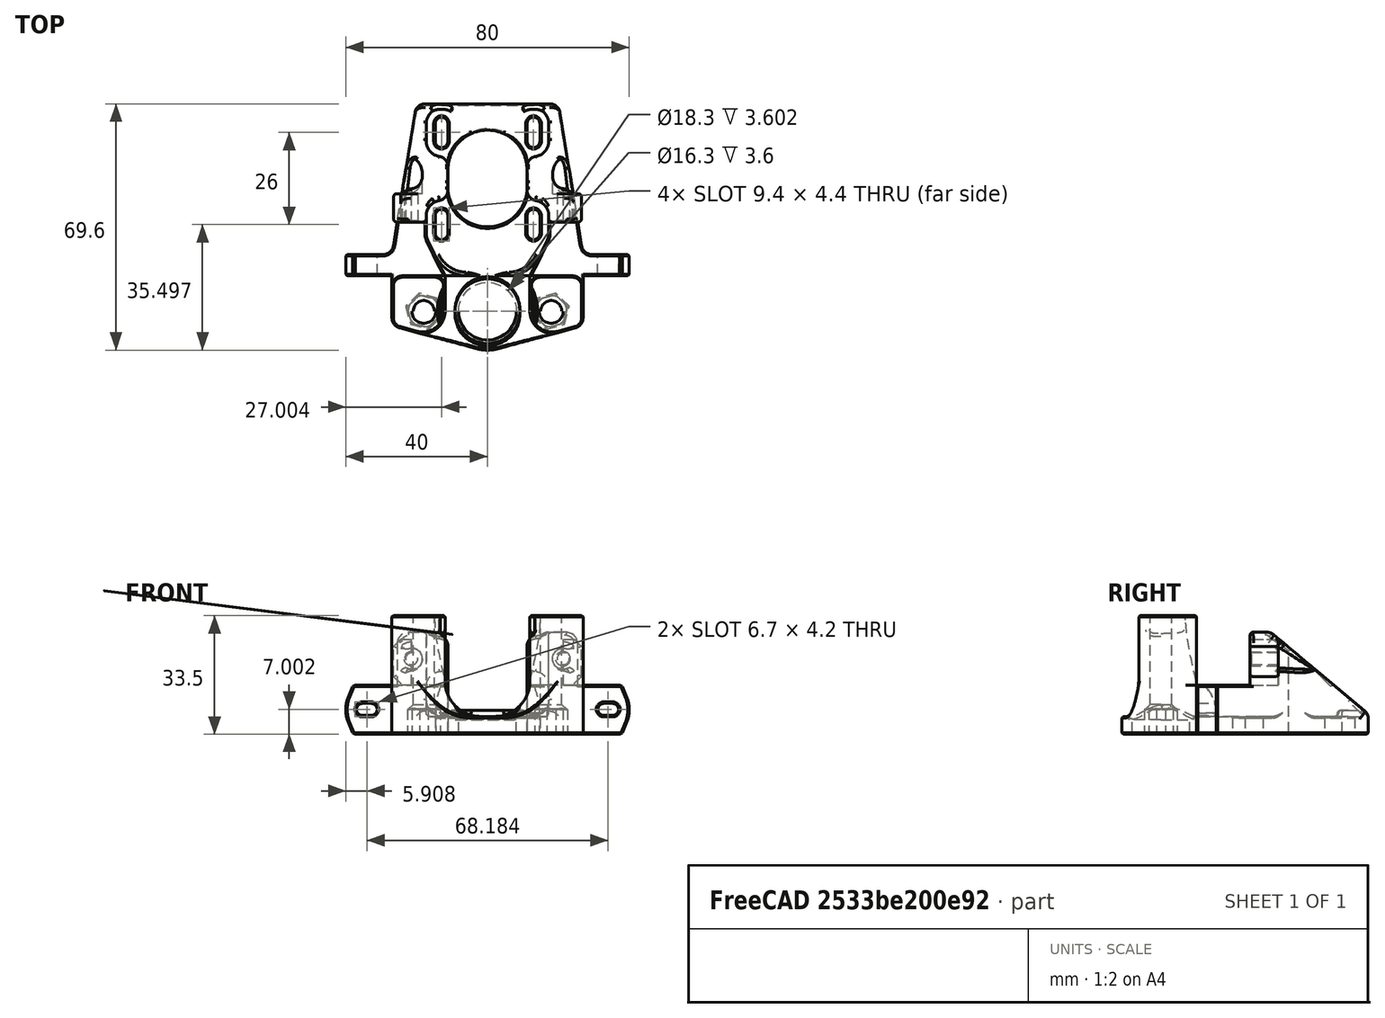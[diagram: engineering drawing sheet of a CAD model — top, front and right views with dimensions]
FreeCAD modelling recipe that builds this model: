
FCSTD DOCUMENT  (FreeCAD 0.18R16146 (Git))
Label: z-motor-mount-rf
License: All rights reserved
LicenseURL: http://en.wikipedia.org/wiki/All_rights_reserved
objects: Part::Box×2, Part::MultiFuse×2, Part::Chamfer×2, Part::Cylinder×2, Part::Feature×1, Part::Fillet×1, Part::Cut×1
note: 11 computed .brp shape members not serialized (recipe doc carries the construction recipe); baked Part::Feature solids carry a one-line shape summary decoded from their .brp

FEATURE [Part::Feature] Part__Feature745  label="Z_Motor_Mount_x1"
  Placement = pos=(-18.0264,-7.72398,-2.89791) rot=(0,0,-1;3.14159rad)
  shape: bbox 80.02 x 83.92 x 33.52 mm, 427 faces (baked)
FEATURE [Part::Box] Box  label="Cube"
  AttacherType = Attacher::AttachEngine3D
  Height = 13
  Length = 5
  Placement = pos=(21,0,13.91) rot=(0,0,1;0rad)
  Width = 8
FEATURE [Part::Box] Box001  label="Cube001"
  AttacherType = Attacher::AttachEngine3D
  Height = 13
  Length = 5
  Placement = pos=(-27,0,13.91) rot=(0,0,1;0rad)
  Width = 8
FEATURE [Part::MultiFuse] Fusion
  Shapes = -> [Box,Box001]
FEATURE [Part::Chamfer] Chamfer
  Base = -> Fusion
  Edges = 2 edges r=2.5: [Edge8,Edge16]
FEATURE [Part::Chamfer] Chamfer001
  Base = -> Chamfer
  Edges = 2 edges r=2: [Edge3,Edge18]
FEATURE [Part::Fillet] Fillet
  Base = -> Chamfer001
  Edges = 14 edges r=0.8: [Edge1,Edge4,Edge5,Edge6,Edge11,Edge13,Edge14,Edge19,Edge22,Edge23,Edge24,Edge29,Edge31,Edge32]
FEATURE [Part::Cylinder] Cylinder
  Angle = 360
  AttacherType = Attacher::AttachEngine3D
  Height = 10
  Placement = pos=(20.9,4.8e-15,21.4) rot=(1,0,0;4.71239rad)
  Radius = 2
FEATURE [Part::Cylinder] Cylinder001
  Angle = 360
  AttacherType = Attacher::AttachEngine3D
  Height = 10
  Placement = pos=(-21.9,5e-15,21.4) rot=(-1,0,0;1.5708rad)
  Radius = 2
FEATURE [Part::MultiFuse] Fusion001
  Placement = pos=(0,-0.6,0) rot=(0,0,1;0rad)
  Shapes = -> [Cylinder001,Cylinder]
FEATURE [Part::Cut] Cut
  Base = -> Fillet
  Tool = -> Fusion001
